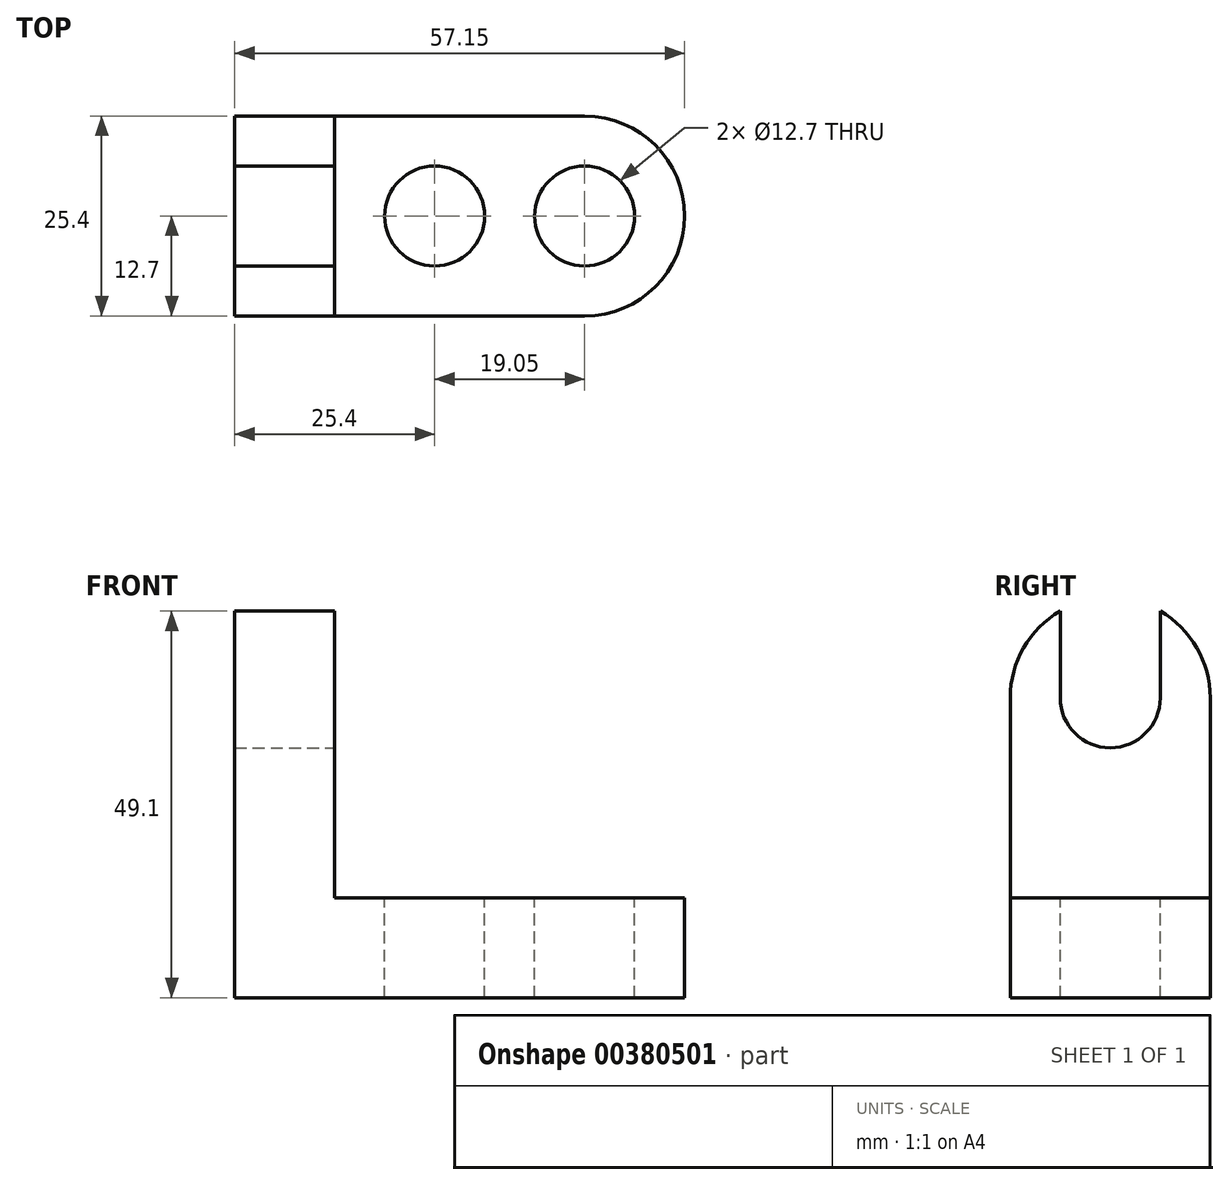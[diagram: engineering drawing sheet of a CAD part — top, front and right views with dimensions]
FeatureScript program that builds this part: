
annotation { "Feature Type Name" : "Feature", "Feature Type Description" : "" }
export const myFeature = defineFeature(function(context is Context, id is Id, definition is map)
    precondition{}
    {
        {
            var Q0;
            Q0=qCreatedBy(makeId("Front.planeOp"),FACE);
            var sketch = newSketch(context, id + "F0", { "sketchPlane" : qUnion([Q0])});
            skLineSegment(sketch, "E0", {"start": v(0, 0) * mm, "end": v(57.15, 0) * mm});
            skLineSegment(sketch, "E1", {"start": v(57.15, 0) * mm, "end": v(57.15, 12.7) * mm});
            skLineSegment(sketch, "E2", {"start": v(57.15, 12.7) * mm, "end": v(12.7, 12.7) * mm});
            skLineSegment(sketch, "E3", {"start": v(12.7, 12.7) * mm, "end": v(12.7, 50.8) * mm});
            skLineSegment(sketch, "E4", {"start": v(12.7, 50.8) * mm, "end": v(0, 50.8) * mm});
            skLineSegment(sketch, "E5", {"start": v(0, 50.8) * mm, "end": v(0, 0) * mm});
            skSolve(sketch);
        }
        {
            var Q0;
            Q0=makeQuery(id+"F0.imprint","IMPRINT",FACE,{"disambiguationData":[TD([[makeQuery(id+"F0.imprint","IMPRINT",EDGE,{"derivedFrom":sQuery(id+"F0.wireOp",EDGE,"E0")}),1.0]])]});
            extrude(context, id + "F1", {"entities" : qUnion([Q0]), "depth" : 25.4 * mm});
        }
        {
            var Q0;
            Q0=makeQuery(id+"F1.opExtrude","SWEPT_FACE",FACE,{"disambiguationData":[OSD([sQuery(id+"F0.wireOp",EDGE,"E3")])]});
            var sketch = newSketch(context, id + "F2", { "sketchPlane" : qUnion([Q0])});
            skCircle(sketch, "E6", {"center": v(-12.7, 38.1) * mm, "radius": 6.35 * mm});
            skLineSegment(sketch, "E7", {"start": v(-19.05, 38.1) * mm, "end": v(-19.05, 50.8) * mm});
            skLineSegment(sketch, "E8", {"start": v(-6.35, 38.1) * mm, "end": v(-6.35, 50.8) * mm});
            skSolve(sketch);
        }
        {
            var Q0;
            {var subQ0=sQuery(id+"F2.wireOp",EDGE,"E7");Q0=makeQuery(id+"F2.imprint","IMPRINT",FACE,{"disambiguationData":[TD([[makeQuery(id+"F2.imprint","IMPRINT",EDGE,{"derivedFrom":subQ0}),-1.0]])]});}
            var Q1;
            {var subQ0=sQuery(id+"F2.wireOp",EDGE,"E6");var subQ1=makeQuery(id+"F2.imprint","INTERSECT",VERTEX,{"derivedFrom":[subQ0,sQuery(id+"F2.wireOp",EDGE,"E7")]});Q1=makeQuery(id+"F2.imprint","IMPRINT",FACE,{"disambiguationData":[TD([[makeQuery(id+"F2.imprint","IMPRINT",EDGE,{"disambiguationData":[TD([[subQ1,1.0]])],"derivedFrom":subQ0}),1.0]])]});}
            extrude(context, id + "F3", {"entities" : qUnion([Q0, Q1]), "operationType" : NewBodyOperationType.REMOVE, "oppositeDirection" : true, "depth" : 12.7 * mm});
        }
        {
            var Q0;
            Q0=makeQuery(id+"F1.opExtrude","SWEPT_FACE",FACE,{"disambiguationData":[OSD([sQuery(id+"F0.wireOp",EDGE,"E3")])]});
            var sketch = newSketch(context, id + "F4", { "sketchPlane" : qUnion([Q0])});
            skArc(sketch, "E9", {"start": v(0, 38.1) * mm, "mid": v(-12.7, 50.8) * mm, "end": v(-25.4, 38.1) * mm});
            skSolve(sketch);
        }
        {
            var Q0;
            {var subQ0=sQuery(id+"F4.wireOp",EDGE,"E9");var subQ1=sQuery(id+"F0.wireOp",EDGE,"E3");var subQ2=makeQuery(id+"F1.opExtrude","CAP_EDGE",EDGE,{"disambiguationData":[OSD([subQ1])],"isStart":false});var subQ3=makeQuery(id+"F4.imprint","INTERSECT",VERTEX,{"derivedFrom":[subQ2,subQ0]});Q0=makeQuery(id+"F4.imprint","IMPRINT",FACE,{"disambiguationData":[TD([[makeQuery(id+"F4.imprint","IMPRINT",EDGE,{"disambiguationData":[TD([[subQ3,1.0]])],"derivedFrom":subQ0}),-1.0]])]});}
            var Q1;
            {var subQ0=sQuery(id+"F4.wireOp",EDGE,"E9");var subQ1=sQuery(id+"F0.wireOp",EDGE,"E3");var subQ2=makeQuery(id+"F1.opExtrude","CAP_EDGE",EDGE,{"disambiguationData":[OSD([subQ1])],"isStart":true});var subQ3=makeQuery(id+"F4.imprint","INTERSECT",VERTEX,{"derivedFrom":[subQ2,subQ0]});Q1=makeQuery(id+"F4.imprint","IMPRINT",FACE,{"disambiguationData":[TD([[makeQuery(id+"F4.imprint","IMPRINT",EDGE,{"disambiguationData":[TD([[subQ3,-1.0]])],"derivedFrom":subQ0}),-1.0]])]});}
            extrude(context, id + "F5", {"entities" : qUnion([Q0, Q1]), "operationType" : NewBodyOperationType.REMOVE, "oppositeDirection" : true, "depth" : 12.7 * mm});
        }
        {
            var Q0;
            Q0=makeQuery(id+"F1.opExtrude","SWEPT_FACE",FACE,{"disambiguationData":[OSD([sQuery(id+"F0.wireOp",EDGE,"E2")])]});
            var sketch = newSketch(context, id + "F6", { "sketchPlane" : qUnion([Q0])});
            skArc(sketch, "E10", {"start": v(44.45, -25.4) * mm, "mid": v(57.15, -12.7) * mm, "end": v(44.45, 0) * mm});
            skSolve(sketch);
        }
        {
            var Q0;
            {var subQ0=sQuery(id+"F6.wireOp",EDGE,"E10");var subQ1=sQuery(id+"F0.wireOp",EDGE,"E2");var subQ2=makeQuery(id+"F1.opExtrude","CAP_EDGE",EDGE,{"disambiguationData":[OSD([subQ1])],"isStart":true});var subQ3=makeQuery(id+"F6.imprint","INTERSECT",VERTEX,{"derivedFrom":[subQ2,subQ0]});Q0=makeQuery(id+"F6.imprint","IMPRINT",FACE,{"disambiguationData":[TD([[makeQuery(id+"F6.imprint","IMPRINT",EDGE,{"disambiguationData":[TD([[subQ3,1.0]])],"derivedFrom":subQ0}),-1.0]])]});}
            var Q1;
            {var subQ0=sQuery(id+"F6.wireOp",EDGE,"E10");var subQ1=sQuery(id+"F0.wireOp",EDGE,"E2");var subQ2=makeQuery(id+"F1.opExtrude","CAP_EDGE",EDGE,{"disambiguationData":[OSD([subQ1])],"isStart":false});var subQ3=makeQuery(id+"F6.imprint","INTERSECT",VERTEX,{"derivedFrom":[subQ2,subQ0]});Q1=makeQuery(id+"F6.imprint","IMPRINT",FACE,{"disambiguationData":[TD([[makeQuery(id+"F6.imprint","IMPRINT",EDGE,{"disambiguationData":[TD([[subQ3,-1.0]])],"derivedFrom":subQ0}),-1.0]])]});}
            extrude(context, id + "F7", {"entities" : qUnion([Q0, Q1]), "operationType" : NewBodyOperationType.REMOVE, "oppositeDirection" : true, "depth" : 12.7 * mm});
        }
        {
            var Q0;
            Q0=makeQuery(id+"F1.opExtrude","SWEPT_FACE",FACE,{"disambiguationData":[OSD([sQuery(id+"F0.wireOp",EDGE,"E2")])]});
            var sketch = newSketch(context, id + "F8", { "sketchPlane" : qUnion([Q0])});
            skCircle(sketch, "E11", {"center": v(44.45, -12.7) * mm, "radius": 6.35 * mm});
            skCircle(sketch, "E12", {"center": v(25.4, -12.7) * mm, "radius": 6.35 * mm});
            skSolve(sketch);
        }
        {
            var Q0;
            Q0=makeQuery(id+"F8.imprint","IMPRINT",FACE,{"disambiguationData":[TD([[makeQuery(id+"F8.imprint","IMPRINT",EDGE,{"derivedFrom":sQuery(id+"F8.wireOp",EDGE,"E11")}),1.0]])]});
            var Q1;
            Q1=makeQuery(id+"F8.imprint","IMPRINT",FACE,{"disambiguationData":[TD([[makeQuery(id+"F8.imprint","IMPRINT",EDGE,{"derivedFrom":sQuery(id+"F8.wireOp",EDGE,"E12")}),1.0]])]});
            extrude(context, id + "F9", {"entities" : qUnion([Q0, Q1]), "operationType" : NewBodyOperationType.REMOVE, "oppositeDirection" : true, "depth" : 12.7 * mm});
        }
    });
